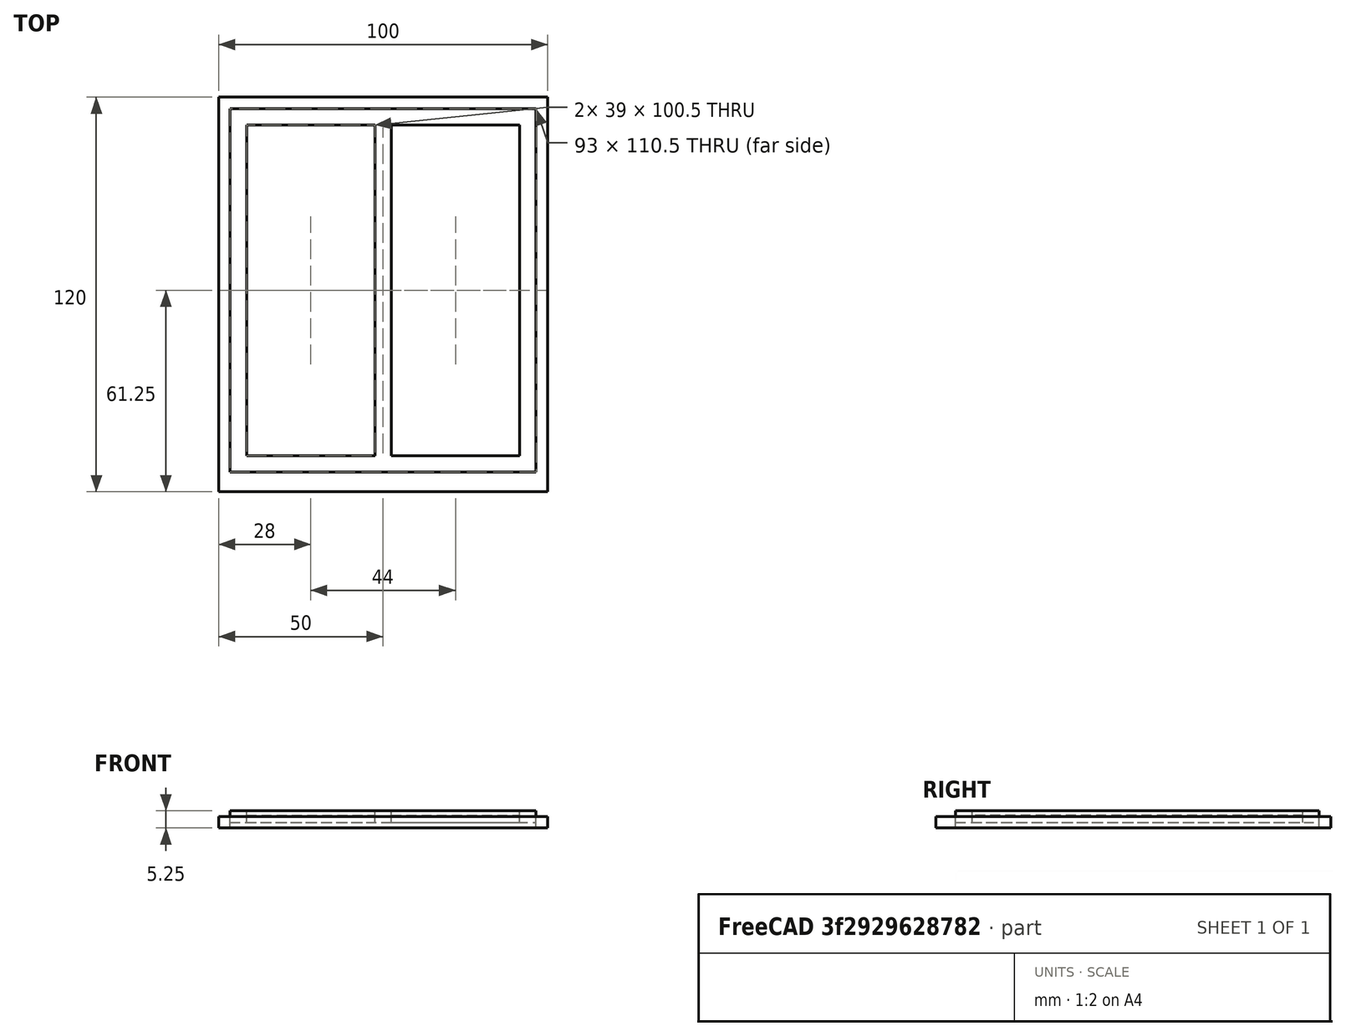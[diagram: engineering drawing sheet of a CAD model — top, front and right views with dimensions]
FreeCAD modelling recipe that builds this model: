
FCSTD DOCUMENT
Label: Simple 2-panes window
License: CC-BY 3.0
LicenseURL: http://creativecommons.org/licenses/by/3.0/
objects: Sketcher::SketchObject×1, Mesh::Feature×1, Part::FeaturePython×1
note: 2 computed .brp shape members not serialized (recipe doc carries the construction recipe); baked Part::Feature solids carry a one-line shape summary decoded from their .brp

FEATURE [Sketcher::SketchObject] Sketch
  sketch-geometry (16):
    g0: LineSegment StartX=0 StartY=0 StartZ=0 EndX=100 EndY=0 EndZ=0
    g1: LineSegment StartX=100 StartY=0 StartZ=0 EndX=100 EndY=120 EndZ=0
    g2: LineSegment StartX=100 StartY=120 StartZ=0 EndX=0 EndY=120 EndZ=0
    g3: LineSegment StartX=0 StartY=120 StartZ=0 EndX=0 EndY=0 EndZ=0
    g4: LineSegment StartX=3.5 StartY=116.5 StartZ=0 EndX=96.5 EndY=116.5 EndZ=0
    g5: LineSegment StartX=96.5 StartY=116.5 StartZ=0 EndX=96.5 EndY=6 EndZ=0
    g6: LineSegment StartX=96.5 StartY=6 StartZ=0 EndX=3.5 EndY=6 EndZ=0
    g7: LineSegment StartX=3.5 StartY=6 StartZ=0 EndX=3.5 EndY=116.5 EndZ=0
    g8: LineSegment StartX=8.5 StartY=111.5 StartZ=0 EndX=47.5 EndY=111.5 EndZ=0
    g9: LineSegment StartX=47.5 StartY=111.5 StartZ=0 EndX=47.5 EndY=11 EndZ=0
    g10: LineSegment StartX=47.5 StartY=11 StartZ=0 EndX=8.5 EndY=11 EndZ=0
    g11: LineSegment StartX=8.5 StartY=11 StartZ=0 EndX=8.5 EndY=111.5 EndZ=0
    g12: LineSegment StartX=52.5 StartY=111.5 StartZ=0 EndX=91.5 EndY=111.5 EndZ=0
    g13: LineSegment StartX=91.5 StartY=111.5 StartZ=0 EndX=91.5 EndY=11 EndZ=0
    g14: LineSegment StartX=91.5 StartY=11 StartZ=0 EndX=52.5 EndY=11 EndZ=0
    g15: LineSegment StartX=52.5 StartY=11 StartZ=0 EndX=52.5 EndY=111.5 EndZ=0
  constraints (48):
    c: Coincident(g0,g1)
    c: Coincident(g1,g2)
    c: Coincident(g2,g3)
    c: Coincident(g3,g0)
    c: Horizontal(g0)
    c: Horizontal(g2)
    c: Vertical(g1)
    c: Vertical(g3)
    c: DistanceX(g0) = 0
    c: DistanceY(g0) = 0
    c: DistanceX(g2,g1) = 100
    c: DistanceY(g1,g0) = -120
    c: Coincident(g4,g5)
    c: Coincident(g5,g6)
    c: Coincident(g6,g7)
    c: Coincident(g7,g4)
    c: Horizontal(g4)
    c: Horizontal(g6)
    c: Vertical(g5)
    c: Vertical(g7)
    c: Coincident(g8,g9)
    c: Coincident(g9,g10)
    c: Coincident(g10,g11)
    c: Coincident(g11,g8)
    c: Horizontal(g8)
    c: Horizontal(g10)
    c: Vertical(g9)
    c: Vertical(g11)
    c: Coincident(g12,g13)
    c: Coincident(g13,g14)
    c: Coincident(g14,g15)
    c: Coincident(g15,g12)
    c: Horizontal(g12)
    c: Horizontal(g14)
    c: Vertical(g13)
    c: Vertical(g15)
    c: DistanceY(g8,g4) = 5
    c: DistanceY(g12,g8) = 0
    c: DistanceX(g4,g8) = 5
    c: DistanceX(g4,g12) = -5
    c: DistanceY(g6,g10) = 5
    c: DistanceY(g9,g14) = 0
    c: DistanceY(g4,g2) = 3.5
    c: DistanceX(g4,g2) = -3.5
    c: DistanceX(g4,g1) = 3.5
    c: DistanceY(g-1,g6) = 6
    c: DistanceX(g8,g12) = 5
    c: Equal(g8,g12)
FEATURE [Mesh::Feature] latch2  label="Latch"
  Placement = pos=(49.1438,64.0559,5.25) rot=(0,0,1;0rad)
FEATURE [Part::FeaturePython] Window  # WARN: FeaturePython — macro-defined, semantics opaque (R4)
  Base = -> Sketch
  Fixtures = -> [latch2]
  WindowParts = Fixed frame | Frame | Wire0,Wire1,Wire2,Wire3 | -3.5 | 0 | Mobile frame | Frame | Wire1,Wire2,Wire3 | 3.5 | 1.75 | Left glass | Glass panel | Wire2 | .3 | 3.5 | Right glass | Glass panel | Wire3 | .3 | 3.5
